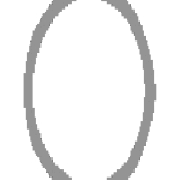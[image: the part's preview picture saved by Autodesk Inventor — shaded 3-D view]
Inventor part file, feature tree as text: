
AUTODESK INVENTOR PART (.ipt)
format: ipt  version: 2021 (Build 250183000, 183)  size: 111,616 bytes
history: native  units: in
note: dims shown in document units (in); Inventor stores cm internally (conversion verified against a paired STEP export)
features: other x4, sketch x3, plane x1
ambient origin geometry x8: Origin, YZ Plane, XZ Plane, XY Plane, X Axis, Y Axis, Z Axis, Center Point
bodies: Solid1 (feature_tree), Body (feature_tree)
feature tree (8):
  other  "Driven Length"
  other  "Frame Generator"
  other  "Start Plane"
  other  "End Plane"
  sketch  "Sketch"  dims[d2=31.6893in d4=-0.0in d5=31.6893in d6=0.12in d7=0.0in d8=90.0deg d9=31.6893in]
  sketch  "Sketch2"  dims[d0=1.0in]
  plane  "Work Plane3"
  sketch  "Sketch3"  dims[d1=0.065in]
